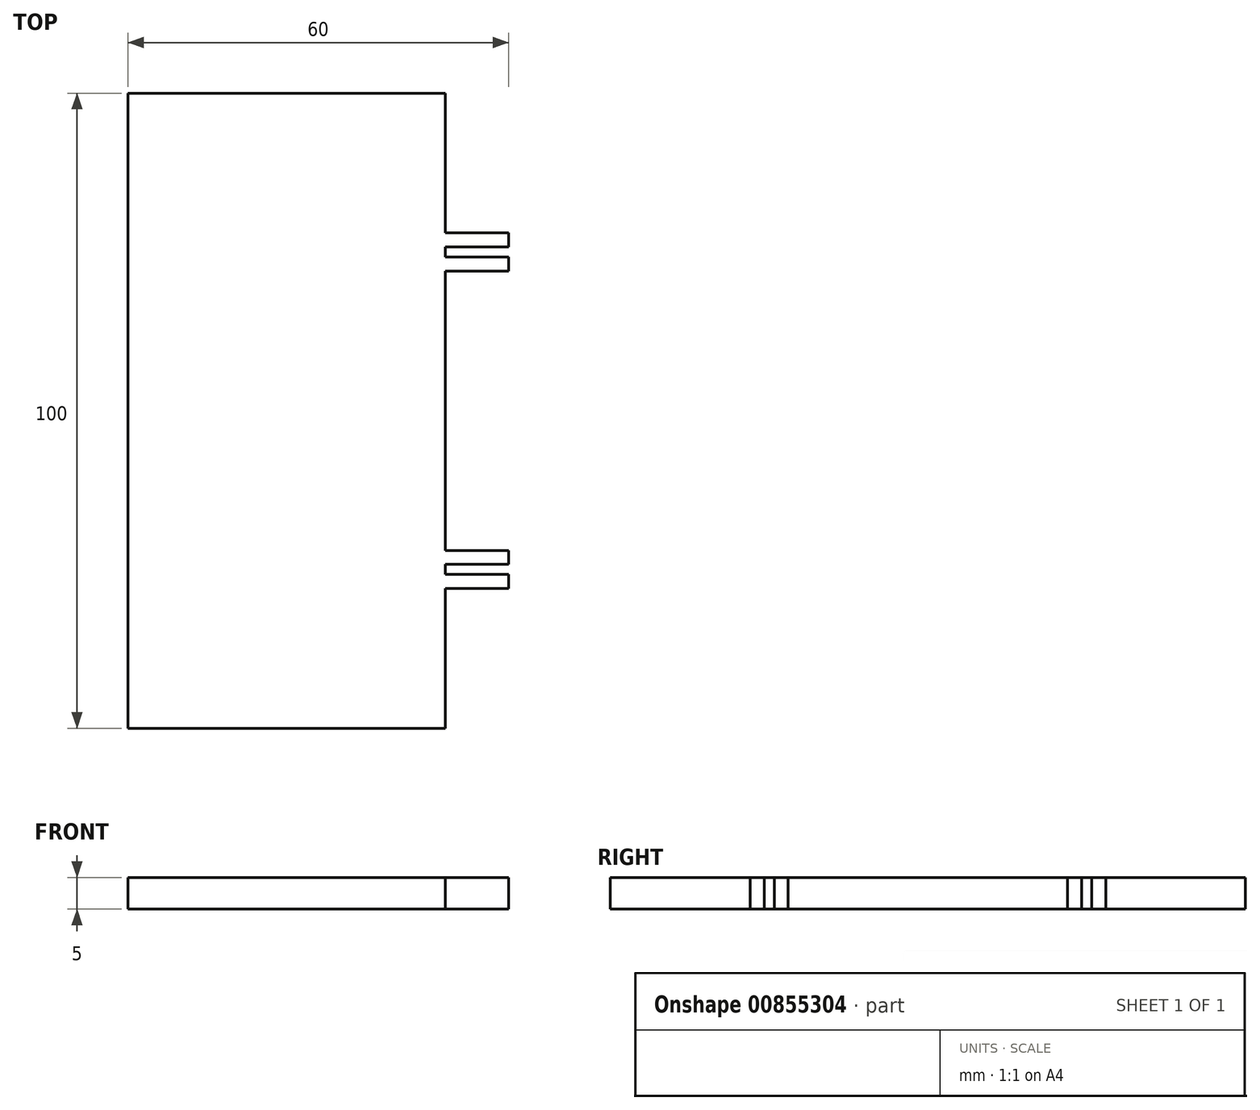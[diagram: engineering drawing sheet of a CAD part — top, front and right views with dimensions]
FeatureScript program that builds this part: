
annotation { "Feature Type Name" : "Feature", "Feature Type Description" : "" }
export const myFeature = defineFeature(function(context is Context, id is Id, definition is map)
    precondition{}
    {
        {
            var Q0;
            Q0=qCreatedBy(makeId("Top.planeOp"),FACE);
            var sketch = newSketch(context, id + "F0", { "sketchPlane" : qUnion([Q0])});
            skLineSegment(sketch, "E0", {"start": v(0, 0) * mm, "end": v(0, 50) * mm});
            skLineSegment(sketch, "E1", {"start": v(0, 0) * mm, "end": v(0, -50) * mm});
            skLineSegment(sketch, "E2", {"start": v(0, 50) * mm, "end": v(50, 50) * mm});
            skLineSegment(sketch, "E3", {"start": v(0, -50) * mm, "end": v(50, -50) * mm});
            skPoint(sketch, "E4", {"position": v(50, 0) * mm});
            skLineSegment(sketch, "E5", {"start": v(50, 0) * mm, "end": v(50, 22) * mm});
            skLineSegment(sketch, "E6", {"start": v(50, 0) * mm, "end": v(50, -22) * mm});
            skLineSegment(sketch, "E7", {"start": v(50, 50) * mm, "end": v(50, 28) * mm});
            skLineSegment(sketch, "E8", {"start": v(50, -50) * mm, "end": v(50, -28) * mm});
            skLineSegment(sketch, "E9", {"start": v(50, 28) * mm, "end": v(60, 28) * mm});
            skLineSegment(sketch, "E10", {"start": v(50, 22) * mm, "end": v(60, 22) * mm});
            skLineSegment(sketch, "E11", {"start": v(50, -22) * mm, "end": v(60, -22) * mm});
            skLineSegment(sketch, "E12", {"start": v(50, -28) * mm, "end": v(60, -28) * mm});
            skLineSegment(sketch, "E13", {"start": v(60, -22) * mm, "end": v(60, -24.2) * mm});
            skLineSegment(sketch, "E14", {"start": v(60, -28) * mm, "end": v(60, -25.8) * mm});
            skLineSegment(sketch, "E15", {"start": v(50, -25.8) * mm, "end": v(60, -25.8) * mm});
            skLineSegment(sketch, "E16", {"start": v(60, -24.2) * mm, "end": v(50, -24.2) * mm});
            skLineSegment(sketch, "E17", {"start": v(50, -24.2) * mm, "end": v(50, -25.8) * mm});
            skLineSegment(sketch, "E18", {"start": v(60, 28) * mm, "end": v(60, 25.8) * mm});
            skLineSegment(sketch, "E19", {"start": v(60, 25.8) * mm, "end": v(50, 25.8) * mm});
            skLineSegment(sketch, "E20", {"start": v(50, 25.8) * mm, "end": v(50, 24.2) * mm});
            skLineSegment(sketch, "E21", {"start": v(50, 24.2) * mm, "end": v(60, 24.2) * mm});
            skLineSegment(sketch, "E22", {"start": v(60, 24.2) * mm, "end": v(60, 22) * mm});
            skSolve(sketch);
        }
        {
            var Q0;
            Q0 = qSketchRegion(id + "F0", true);
            extrude(context, id + "F1", {"entities" : qUnion([Q0]), "depth" : 5 * mm, "offsetDistance" : 25 * mm});
        }
    });
